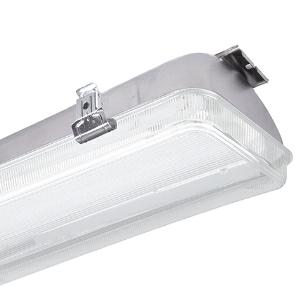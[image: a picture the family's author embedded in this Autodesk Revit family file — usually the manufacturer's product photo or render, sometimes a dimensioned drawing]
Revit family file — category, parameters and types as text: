
# Revit family: 3f_filippi_-_beta_235_92_pc_ampio_3f_filippi_-_52939_-_beta_235_led_922x15_ampio_l655
name_source: partatom
category: Lighting Fixtures
units: mm (PartAtom-declared; Revit-internal decimal feet)

## family parameters
Cut with Voids When Loaded = No
Host = Face
Light Source = No
Part Type = Normal
Room Calculation Point = No
Round Connector Dimension = Use Diameter
Shared = No

## types (1)
- 3F Filippi - Beta 235 92 PC Ampio (1 x LED, 5175 lm, 34 W, 4000 K)
    Apparent Load = 34 VA
    Approval mark = CE
    CIE Flux Codes = 59 89 98 98 100
    Color Rendering = 80
    Color Temperature = 4000 K
    Control Gear = Electronic ballast
    Default Elevation = 1800 mm
    Description = ILLUMINOTECHNICAL
Luminous efficiency 100% (DLOR 99%, ULOR 1%).
Initial luminous flux of the luminaire 5175 lm.
Wide symmetric distribution.
Installation Interdistance Transv.D = 1.40 x hu - Long.D = 1.43 x hu.
Tabular UGR (CIE 117 - 4H-8H; S=0.25H; 70/50/20): RUG 20 - 20.4.
Beam angle: 98° - 100°.
Luminous efficacy 152 lm/W.
Lifetime (L93/B10): 30000 h. (tq+25°C)
Lifetime (L90/B10): 50000 h. (tq+25°C)
Lifetime (L85/B10): 80000 h. (tq+25°C)
Lifetime (L80/B10): 100000 h. (tq+25°C)
Lifetime (L85/B10): 50000 h. (tq+45°C)
Sudden decreased luminous flux after 50000 hours: 0% (C0).
Photobiological safety in compliance with IEC/TR 62778: RG0 risk exempt, (IEC 62471).
In compliance with IEC/EN 62722-2-1 - IEC/EN 62717 standards.

SOURCE
2 linear LED modules 15W/840.
Energy efficiency class (UE 2019/2020 - UE 2019/2015): C.
CIE 13.3 Colour rendering index: CRI >80 (R9 <50%).
IES TM-30 Fidelity Index: Rf = 84 Rg = 95.
CCT nominal colour temperature 4000 K.
Colour initial tolerance (MacAdam): SDCM 3.

MECHANICAL
Housing in AISI 304 stainless steel, pressed in one single piece.
Polycarbonate screen etched internally, V2 self-extinguishing, UV stabilised, injection moulded.
Ecologic anti-aging sealing gasket.
Oversized gear-tray reflector unit in highly reflective white painted hot-galvanised steel.
Methacrylate (PMMA) lenses with external flat surface.
Stainless steel safety snap-lock clips for diffuser mounting.
Luminaire with limited surface temperature. - D - (EN 60598-2-24)
Dimensions: 655x235 mm, height 140 mm. Weight 3.93 kg.
IP65 protection degree.
Mechanical strength to impacts IK10 (20 joule).
Glow-wire test resistance 850°C.

ELECTRICAL
Halogen Free electronic wiring 230V-50/60Hz, power factor 0.90, THD <25%, constant output current, class I, 1 driver.
Power of the luminaire 34 W.
ENEC - CE.
Flicker: <4%.
Luminaire compliant with EN 60598-2-22 for power supply from a centralised emergency system CPSS (Central Power Supply System), not incorporated in the luminaire - high risk areas excluded. The default power and flux are 100% in AC and 100% in DC.
Ambient temperature from -20°C to +45°C.
Temperature class T6 max 85°C.
Quick connection via M20 3P connector with 9-13 mm tightening range.
Relative humidity UR: <85%.

INSTALLATION
Ceiling / Suspended / Wall.
All accessories dedicated to this product are available on the Catalog and on our website www.3F-Filippi.com.

APPLICATIONS
Suitable product for food production plants (HACCP), IFS (Food Version 6), BRC (GSFS Food Version 7).
Dry, dusty indoor environments, subject to occasional water splashes.
Any environments except the ones where the luminaire materials are unsuitable.
Industrial environments, warehouses, environments where security locks are required on all clips, e.g. prisons.
Environments in which it is necessary a total protection against falling fragments (eg environments with foodstuffs or machines with moving parts or with extreme temperature changes), use luminaires with laminated glass.
Tempered glass is not immune to falling fragments from harmless and caused by shocks or exceptionally derived from the tempering process.

WARNING
Fixture not suitable for cold stores with an ambient temperature <0°C and/or relative humidity >85%.
Luminaire designed for disposal/recycling at end-of-life.
Replaceable (LED only) light source by a professional. Replaceable control gear by a professional.
    Height = 140 mm  [stored 0.459318 ft]
    Lamp = 1 x LED
    Lamp Light Flux = 5175 lm
    Lamp Power = 34 W
    Lamp count = 1
    Length = 655 mm
    Lifetime = 50000 h
    Luminous efficacy = 152 lm/W
    Manufacturer = 3F Filippi
    ModVariant = No
    Model = 3F Filippi - 52939 - Beta 235 LED 922x15 AMPIO L655
    Mounting Place = Ceiling
    Mounting Type = Pendant
    Number of Poles = 1
    OnlyDefault = Yes
    Power Factor = 1
    Product Name = 3F Filippi - Beta 235 92 PC Ampio
    Product group = pendant luminaire
    ProductGroupID = 9
    Protection Class = Protection class I
    Protection Degree = IP 65
    RLX_Detail_Level = 1
    RLX_Emergency_Light_Flux = 0 lm
    RLX_Emergency_Type = 0
    RLX_Emergency_Type_DB = No
    RlxData = <blob elided: 89265 chars, md5=9c2fe18c>
    Socket = socket
    Standby Power = 0 W
    System Light Flux = 5175 lm
    System Power = 34 W
    Type Comments = Product without accessories
    Type Image = 3ffilippi_52939.jpg
    URL = http://relux.com
    VarID = ---
    Voltage = 0 V
    Weight = 0.00 kg
    Width = 235 mm

note: [stored X ft] marks values corroborated as IEEE doubles in the binary element streams (Revit-internal decimal feet)

## geometry (parser evidence)
native form markers: Blend x4, Sweep x9
no freeform markers — native parametric forms only
